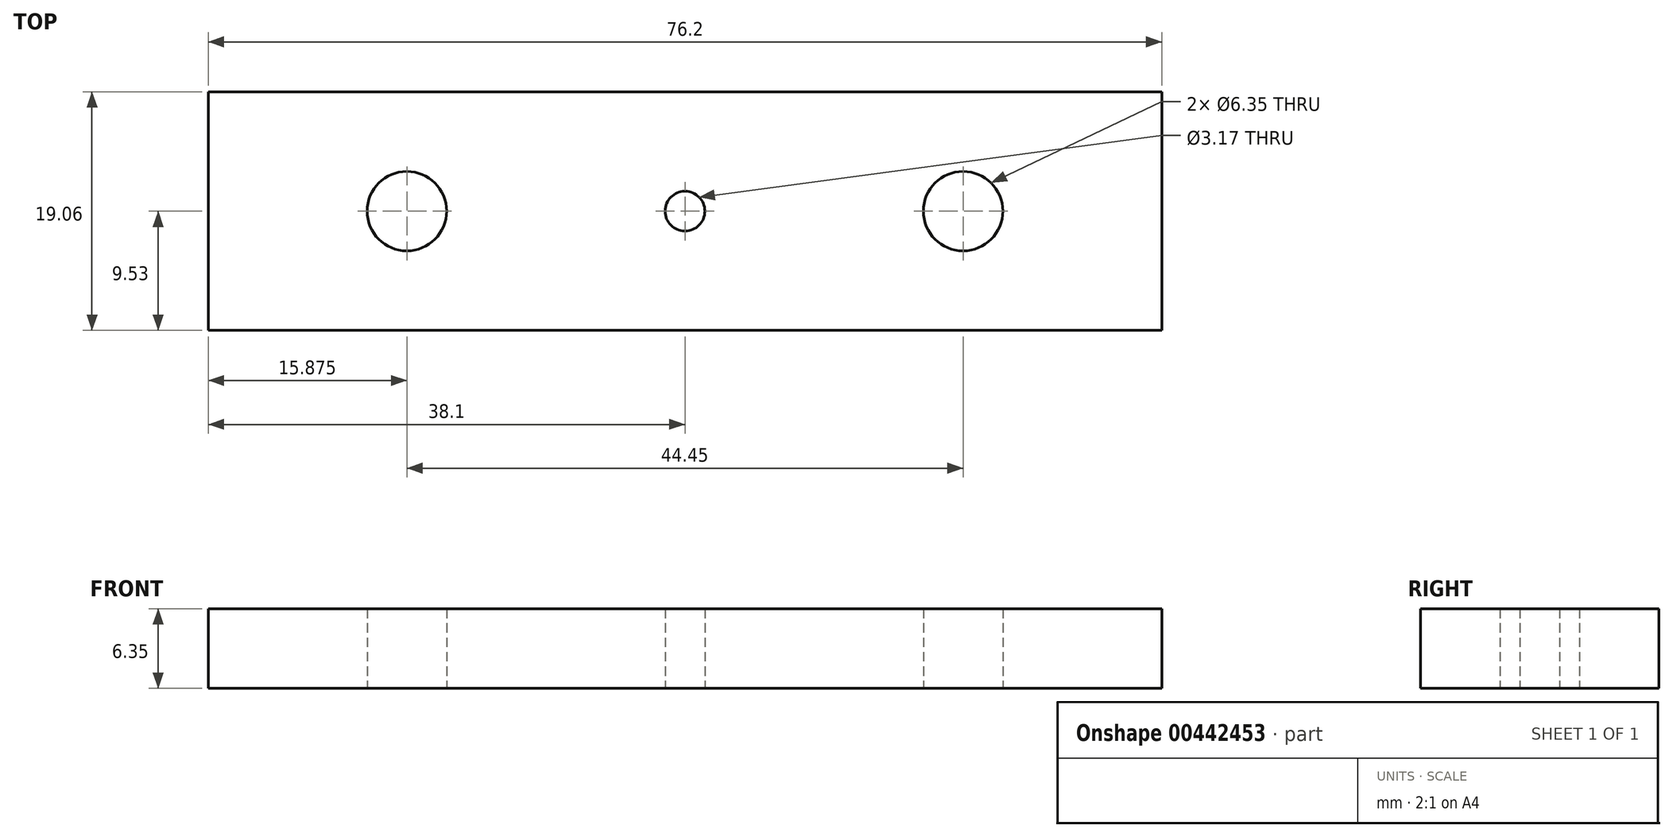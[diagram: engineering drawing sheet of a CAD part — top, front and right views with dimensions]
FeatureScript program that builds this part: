
annotation { "Feature Type Name" : "Feature", "Feature Type Description" : "" }
export const myFeature = defineFeature(function(context is Context, id is Id, definition is map)
    precondition{}
    {
        {
            var Q0;
            Q0=qCreatedBy(makeId("Top.planeOp"),FACE);
            var sketch = newSketch(context, id + "F0", { "sketchPlane" : qUnion([Q0])});
            skLineSegment(sketch, "E0.bottom", {"start": v(38.1, 9.53) * mm, "end": v(-38.1, 9.53) * mm});
            skLineSegment(sketch, "E0.top", {"start": v(38.1, -9.53) * mm, "end": v(-38.1, -9.53) * mm});
            skLineSegment(sketch, "E0.left", {"start": v(38.1, 9.53) * mm, "end": v(38.1, -9.52) * mm});
            skLineSegment(sketch, "E0.right", {"start": v(-38.1, 9.53) * mm, "end": v(-38.1, -9.52) * mm});
            skPoint(sketch, "E0.middle", {"position": v(0, 0) * mm});
            skCircle(sketch, "E1", {"center": v(22.23, 0) * mm, "radius": 3.18 * mm});
            skCircle(sketch, "E2", {"center": v(-22.23, 0) * mm, "radius": 3.18 * mm});
            skCircle(sketch, "E3", {"center": v(0, 0) * mm, "radius": 1.59 * mm});
            skSolve(sketch);
        }
        {
            var Q0;
            Q0 = qSketchRegion(id + "F0", true);
            extrude(context, id + "F1", {"entities" : qUnion([Q0]), "depth" : 6.35 * mm});
        }
    });
